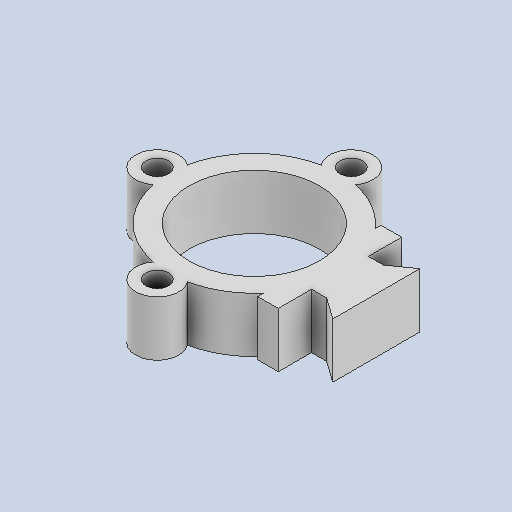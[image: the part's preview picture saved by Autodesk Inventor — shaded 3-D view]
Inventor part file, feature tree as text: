
AUTODESK INVENTOR PART (.ipt)
format: ipt  version: 2024 (Build 280153000, 153)  size: 140,800 bytes
history: native  units: mm
features: other x4, sketch x1
ambient origin geometry x8: Origin, YZ Plane, XZ Plane, XY Plane, X Axis, Y Axis, Z Axis, Center Point
bodies: Body1 (feature_tree)
feature tree (5):
  other  "acople_v2.ipt"
  other  "Sólido1::acople_v2.ipt"
  other  "OperaciónIdentificador1"
  sketch  "Boceto1"  dims[d0=10.0mm]
  other  "Sólido1"
